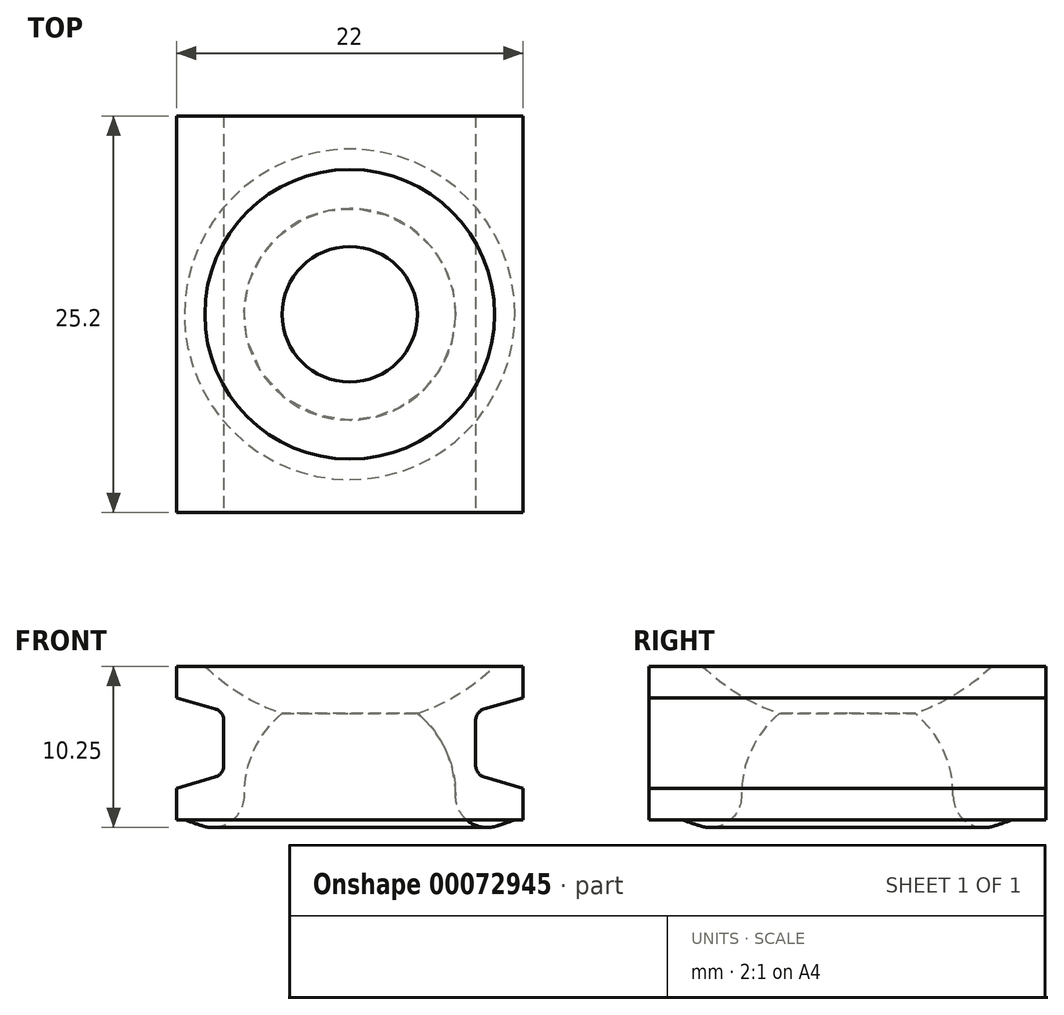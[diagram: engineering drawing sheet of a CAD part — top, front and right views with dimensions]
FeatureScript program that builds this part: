
annotation { "Feature Type Name" : "Feature", "Feature Type Description" : "" }
export const myFeature = defineFeature(function(context is Context, id is Id, definition is map)
    precondition{}
    {
        {
            var Q0;
            Q0=qCreatedBy(makeId("Top.planeOp"),FACE);
            var sketch = newSketch(context, id + "F0", { "sketchPlane" : qUnion([Q0])});
            skLineSegment(sketch, "E0.rect.bottom", {"start": v(11, 12.6) * mm, "end": v(-11, 12.6) * mm});
            skLineSegment(sketch, "E0.rect.top", {"start": v(11, -12.6) * mm, "end": v(-11, -12.6) * mm});
            skLineSegment(sketch, "E0.rect.left", {"start": v(11, 12.6) * mm, "end": v(11, -12.6) * mm});
            skLineSegment(sketch, "E0.rect.right", {"start": v(-11, 12.6) * mm, "end": v(-11, -12.6) * mm});
            skPoint(sketch, "E0.rect.middle", {"position": v(0, 0) * mm});
            skSolve(sketch);
        }
        {
            var Q0;
            Q0 = qSketchRegion(id + "F0", true);
            extrude(context, id + "F1", {"entities" : qUnion([Q0]), "depth" : 9.75 * mm});
        }
        {
            var Q0;
            Q0=makeQuery(id+"F1.opExtrude","SWEPT_FACE",FACE,{"disambiguationData":[OSD([sQuery(id+"F0.wireOp",EDGE,"E0.rect.top")])]});
            var sketch = newSketch(context, id + "F2", { "sketchPlane" : qUnion([Q0])});
            skLineSegment(sketch, "E1", {"start": v(-8, 6.88) * mm, "end": v(-8, 2.88) * mm});
            skLineSegment(sketch, "E2", {"start": v(-11, 2) * mm, "end": v(-11, 7.75) * mm});
            skLineSegment(sketch, "E3", {"start": v(-8, 6.88) * mm, "end": v(-11, 7.75) * mm});
            skLineSegment(sketch, "E4", {"start": v(-8, 2.88) * mm, "end": v(-11, 2) * mm});
            skLineSegment(sketch, "E5", {"start": v(0, 9.75) * mm, "end": v(0, 0) * mm, "construction": true});
            skLineSegment(sketch, "E6.MirrorCS", {"start": v(8, 6.88) * mm, "end": v(11, 7.75) * mm});
            skLineSegment(sketch, "E7.MirrorCS", {"start": v(8, 2.88) * mm, "end": v(11, 2) * mm});
            skLineSegment(sketch, "E8.MirrorCS", {"start": v(11, 2) * mm, "end": v(11, 7.75) * mm});
            skLineSegment(sketch, "E9.MirrorCS", {"start": v(8, 6.88) * mm, "end": v(8, 2.88) * mm});
            skSolve(sketch);
        }
        {
            var Q0;
            Q0 = qSketchRegion(id + "F2", true);
            var Q1;
            Q1=makeQuery(id+"F1.opExtrude","SWEPT_FACE",FACE,{"disambiguationData":[OSD([sQuery(id+"F0.wireOp",EDGE,"E0.rect.bottom")])]});
            extrude(context, id + "F3", {"entities" : qUnion([Q0]), "operationType" : NewBodyOperationType.REMOVE, "endBound" : BoundingType.UP_TO_SURFACE, "oppositeDirection" : true, "endBoundEntityFace" : qUnion([Q1]), "depth" : 25 * mm});
        }
        {
            var Q0;
            Q0=qCreatedBy(makeId("Right.planeOp"),FACE);
            var sketch = newSketch(context, id + "F4", { "sketchPlane" : qUnion([Q0])});
            skLineSegment(sketch, "E10", {"start": v(0, 6.75) * mm, "end": v(4.3, 6.75) * mm});
            skLineSegment(sketch, "E11", {"start": v(0, 9.75) * mm, "end": v(9.2, 9.75) * mm});
            skArc(sketch, "E12", {"start": v(4.3, 6.75) * mm, "mid": v(6.91, 7.98) * mm, "end": v(9.2, 9.75) * mm});
            skLineSegment(sketch, "E13", {"start": v(0, 9.75) * mm, "end": v(0, 6.75) * mm});
            skSolve(sketch);
        }
        {
            var Q0;
            Q0 = qSketchRegion(id + "F4", true);
            var Q1;
            Q1=sQuery(id+"F4.wireOp",EDGE,"E13");
            revolve(context, id + "F5", {"operationType" : NewBodyOperationType.REMOVE, "entities" : qUnion([Q0]), "axis" : qUnion([Q1]), "revolveType" : RevolveType.FULL, "oppositeDirection" : true});
        }
        {
            var Q0;
            Q0=qCreatedBy(makeId("Front.planeOp"),FACE);
            var sketch = newSketch(context, id + "F6", { "sketchPlane" : qUnion([Q0])});
            skArc(sketch, "E14", {"start": v(6.1, -1.25) * mm, "mid": v(5.67, 5.2) * mm, "end": v(0, 8.3) * mm});
            skLineSegment(sketch, "E15", {"start": v(0, 8.3) * mm, "end": v(0, -1.25) * mm});
            skLineSegment(sketch, "E16", {"start": v(0, -1.25) * mm, "end": v(6.1, -1.25) * mm});
            skSolve(sketch);
        }
        {
            var Q0;
            Q0 = qSketchRegion(id + "F6", true);
            var Q1;
            Q1=sQuery(id+"F6.wireOp",EDGE,"E15");
            revolve(context, id + "F7", {"operationType" : NewBodyOperationType.REMOVE, "entities" : qUnion([Q0]), "axis" : qUnion([Q1]), "revolveType" : RevolveType.FULL, "oppositeDirection" : true});
        }
        {
            var Q0;
            Q0=qCreatedBy(makeId("Front.planeOp"),FACE);
            var sketch = newSketch(context, id + "F8", { "sketchPlane" : qUnion([Q0])});
            skArc(sketch, "E17", {"start": v(6.1, -1.25) * mm, "mid": v(6.35, -0.64) * mm, "end": v(6.54, 0) * mm});
            skLineSegment(sketch, "E18", {"start": v(6.54, 0) * mm, "end": v(10.5, 0) * mm});
            skArc(sketch, "E19", {"start": v(6.1, -1.25) * mm, "mid": v(8.32, -0.7) * mm, "end": v(10.5, 0) * mm});
            skLineSegment(sketch, "E20", {"start": v(10.5, 0) * mm, "end": v(6.54, 0) * mm});
            skPoint(sketch, "E21.end.orphan", {"position": v(6.1, -1.25) * mm});
            skPoint(sketch, "E21.start.orphan", {"position": v(0, -1.25) * mm});
            skLineSegment(sketch, "E22", {"start": v(0, 0) * mm, "end": v(0, -8.8) * mm});
            skSolve(sketch);
        }
        {
            var Q0;
            Q0=qCreatedBy(makeId("Front.planeOp"),FACE);
            var sketch = newSketch(context, id + "F9", { "sketchPlane" : qUnion([Q0])});
            skLineSegment(sketch, "E23", {"start": v(0, 14.64) * mm, "end": v(0, -7.66) * mm});
            skSolve(sketch);
        }
        {
            var Q0;
            Q0 = qSketchRegion(id + "F6", true);
            var Q1;
            Q1=sQuery(id+"F9.wireOp",EDGE,"E23");
            revolve(context, id + "F10", {"operationType" : NewBodyOperationType.REMOVE, "entities" : qUnion([Q0]), "axis" : qUnion([Q1]), "revolveType" : RevolveType.FULL, "oppositeDirection" : true});
        }
        {
            var Q0;
            Q0=makeQuery(id+"F8.imprint","IMPRINT",FACE,{"disambiguationData":[TD([[makeQuery(id+"F8.imprint","IMPRINT",EDGE,{"derivedFrom":sQuery(id+"F8.wireOp",EDGE,"E17")}),-1.0]])]});
            var Q1;
            Q1=sQuery(id+"F6.wireOp",EDGE,"E15");
            revolve(context, id + "F11", {"operationType" : NewBodyOperationType.ADD, "entities" : qUnion([Q0]), "axis" : qUnion([Q1]), "revolveType" : RevolveType.FULL});
        }
        {
            var Q0;
            Q0=makeQuery(id+"F11.opRevolve","SWEPT_EDGE",EDGE,{"disambiguationData":[OSD([sQuery(id+"F8.wireOp",EDGE,"E19"),sQuery(id+"F8.wireOp",EDGE,"E20")])]});
            fillet(context, id + "F12", {"entities" : qUnion([Q0]), "radius" : 2 * mm, "tangentPropagation" : true, "allowEdgeOverflow" : false});
        }
        {
            var Q0;
            Q0=makeQuery(id+"F3.boolean.opBoolean","COPY",EDGE,{"derivedFrom":makeQuery(id+"F3.opExtrude","SWEPT_EDGE",EDGE,{"disambiguationData":[OSD([sQuery(id+"F2.wireOp",EDGE,"E7.MirrorCS"),sQuery(id+"F2.wireOp",EDGE,"E9.MirrorCS")])]})});
            var Q1;
            Q1=makeQuery(id+"F3.boolean.opBoolean","COPY",EDGE,{"derivedFrom":makeQuery(id+"F3.opExtrude","SWEPT_EDGE",EDGE,{"disambiguationData":[OSD([sQuery(id+"F2.wireOp",EDGE,"E6.MirrorCS"),sQuery(id+"F2.wireOp",EDGE,"E9.MirrorCS")])]})});
            var Q2;
            Q2=makeQuery(id+"F3.boolean.opBoolean","COPY",EDGE,{"derivedFrom":makeQuery(id+"F3.opExtrude","SWEPT_EDGE",EDGE,{"disambiguationData":[OSD([sQuery(id+"F2.wireOp",EDGE,"E1"),sQuery(id+"F2.wireOp",EDGE,"E3")])]})});
            var Q3;
            Q3=makeQuery(id+"F3.boolean.opBoolean","COPY",EDGE,{"derivedFrom":makeQuery(id+"F3.opExtrude","SWEPT_EDGE",EDGE,{"disambiguationData":[OSD([sQuery(id+"F2.wireOp",EDGE,"E1"),sQuery(id+"F2.wireOp",EDGE,"E4")])]})});
            fillet(context, id + "F13", {"entities" : qUnion([Q0, Q1, Q2, Q3]), "radius" : 0.75 * mm, "tangentPropagation" : true, "allowEdgeOverflow" : false});
        }
    });
